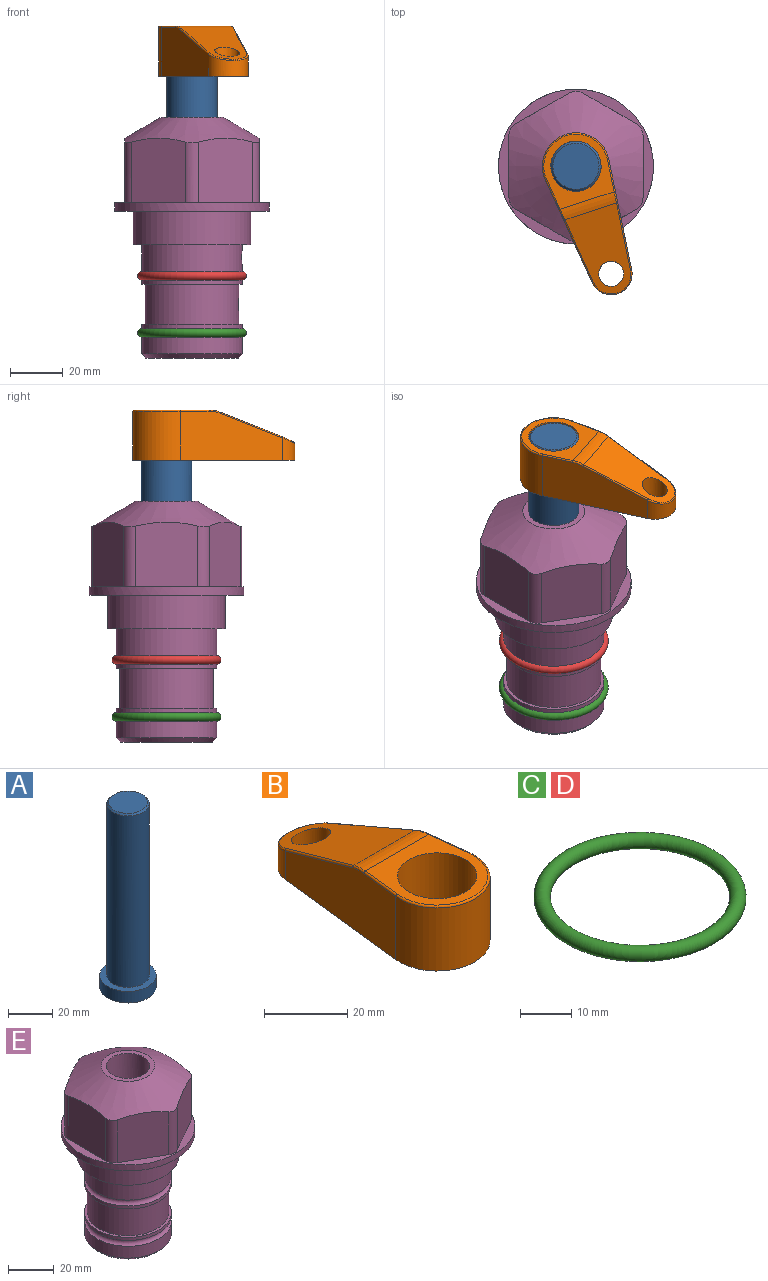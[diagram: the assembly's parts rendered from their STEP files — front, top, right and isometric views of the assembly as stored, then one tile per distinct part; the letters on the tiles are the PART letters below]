
ASSEMBLY  parts=5 mates=3
PART A: 6 faces, bbox 25.4x25.4x101.6 mm
  f0: plane 17.46x17.46mm, normal (0,0,1), area 239.5mm2, adj f5
  f1: plane 25.4x25.4mm, normal (0,0,-1), area 506.7mm2, adj f2
  f2: cylinder r=12.7mm len=25.4mm, axis (0,0,1), area 506.7mm2, adj f1,f3
  f3: plane 25.4x25.4mm, normal (0,0,1), area 221.7mm2, adj f2,f4
  f4: cylinder r=9.53mm len=94.46mm, axis (0,0,1), area 5653mm2, adj f3,f5
  f5: cone r=8.73mm half-angle=45deg, axis (0,0,-1), area 64.4mm2, adj f0,f4
PART B: 44 faces, bbox 27.5x64.5x19.1 mm
  f0: plane 2.3x0.95mm, normal (0,0,-1), area 1mm2, adj f25,f30,f34
  f1: plane 63.5x25.4mm, normal (0,0,-1), area 561.7mm2, adj f2,f3,f4,f5,f6,f7,f19,f20
  f2: cylinder r=12.7mm len=25.4mm, axis (0,0,-1), area 792.2mm2, adj f1,f3,f5,f13
  f3: plane 42.33x18.54mm, normal (0.99,0.11,0), area 647mm2, adj f1,f2,f4,f11,f12,f14
  f4: cylinder r=7.94mm len=15.78mm, axis (0,0,-1), area 158.6mm2, adj f1,f3,f5,f16
  f5: plane 42.33x18.54mm, normal (-0.99,0.11,0), area 647mm2, adj f1,f2,f4,f15,f17,f18
  f6: cylinder r=9.53mm len=19.05mm, axis (0,0,-1), area 1140.1mm2, adj f1,f8
  f7: cylinder r=4.76mm len=10.98mm, axis (0,0,-1), area 276.1mm2, adj f1,f9
  f8: plane 25.83x24.38mm, normal (0,0,1), area 262.2mm2, adj f6,f10,f11,f13,f15
  f9: plane 32.49x20.55mm, normal (0,0.34,0.94), area 489.9mm2, adj f7,f10,f14,f16,f18
  f10: cylinder r=12.7mm len=21.49mm, axis (-1,0,0), area 93.2mm2, adj f8,f9,f12,f17
  f11: cylinder r=0.51mm len=12.34mm, axis (0.11,-0.99,0), area 9.9mm2, adj f3,f8,f12,f13
  f12: bspline ~7.62x1.64mm, area 3.5mm2, adj f3,f10,f11,f14
  f13: torus R=12.19mm, axis (0,0,1), area 33.6mm2, adj f2,f8,f11,f15
  f14: cylinder r=0.51mm len=26.01mm, axis (0.1,-0.93,0.34), area 21.6mm2, adj f3,f9,f12,f16
  f15: cylinder r=0.51mm len=12.34mm, axis (0.11,0.99,0), area 9.9mm2, adj f5,f8,f13,f17
  f16: bspline ~15.78x7.05mm, area 15.7mm2, adj f4,f9,f14,f18
  f17: bspline ~7.62x1.64mm, area 3.5mm2, adj f5,f10,f15,f18
  f18: cylinder r=0.51mm len=26.01mm, axis (0.1,0.93,-0.34), area 21.6mm2, adj f5,f9,f16,f17
  f19: plane 21.6x14.29mm, normal (-0.99,-0.11,0), area 242.6mm2, adj f1,f26,f28,f34,f36,f38
  f20: plane 21.6x14.29mm, normal (0.99,-0.11,0), area 242.6mm2, adj f1,f27,f29,f37,f39,f41
  f21: cylinder r=12.7mm len=14.29mm, axis (0,0,-1), area 173.2mm2, adj f1,f26,f27,f30,f31,f33
  f22: cylinder r=7.94mm len=7.63mm, axis (0,0,-1), area 53.8mm2, adj f1,f28,f29,f42
  f23: plane 2.3x0.95mm, normal (0,0,-1), area 1mm2, adj f25,f33,f37
  f24: plane 17.94x12.32mm, normal (0,-0.34,-0.94), area 191.2mm2, adj f25,f38,f41,f42
  f25: cylinder r=9.53mm len=12.93mm, axis (-1,0,0), area 37.5mm2, adj f0,f23,f24,f31,f36,f39
  f26: cylinder r=1.59mm len=14.29mm, axis (0,0,-1), area 49mm2, adj f1,f19,f21,f32
  f27: cylinder r=1.59mm len=14.29mm, axis (0,0,-1), area 49mm2, adj f1,f20,f21,f35
  f28: cylinder r=1.59mm len=7.28mm, axis (0,0,-1), area 22.1mm2, adj f1,f19,f22,f40
  f29: cylinder r=1.59mm len=7.28mm, axis (0,0,-1), area 22.1mm2, adj f1,f20,f22,f43
  f30: torus R=14.29mm, axis (0,0,1), area 5.8mm2, adj f0,f21,f31,f32
  f31: bspline ~11.06x2.73mm, area 20.8mm2, adj f21,f25,f30,f33
  f32: sphere r=1.59mm, area 5.4mm2, adj f26,f30,f34
  f33: torus R=14.29mm, axis (0,0,1), area 5.8mm2, adj f21,f23,f31,f35
  f34: cylinder r=1.59mm len=1.68mm, axis (-0.11,0.99,0), area 2.4mm2, adj f0,f19,f32,f36
  f35: sphere r=1.59mm, area 5.4mm2, adj f27,f33,f37
  f36: bspline ~5.82x2.33mm, area 7.7mm2, adj f19,f25,f34,f38
  f37: cylinder r=1.59mm len=1.68mm, axis (0.11,0.99,0), area 2.4mm2, adj f20,f23,f35,f39
  f38: cylinder r=1.59mm len=18.33mm, axis (0.1,-0.93,0.34), area 46.7mm2, adj f19,f24,f36,f40
  f39: bspline ~5.82x2.33mm, area 7.7mm2, adj f20,f25,f37,f41
  f40: sphere r=1.59mm, area 3.6mm2, adj f28,f38,f42
  f41: cylinder r=1.59mm len=18.33mm, axis (0.1,0.93,-0.34), area 46.7mm2, adj f20,f24,f39,f43
  f42: bspline ~8.31x1.84mm, area 15.3mm2, adj f22,f24,f40,f43
  f43: sphere r=1.59mm, area 3.6mm2, adj f29,f41,f42
PART C: 1 faces, bbox 44.7x44.7x3.2 mm
  f0: torus R=19.05mm, axis (0,0,1), area 1193.9mm2
PART D: same geometry as C
PART E: 36 faces, bbox 58.7x58.7x91.2 mm
  f0: cylinder r=17.78mm len=35.56mm, axis (0,0,1), area 1670.8mm2, adj f23,f24,f31
  f1: cylinder r=19.05mm len=38.1mm, axis (0,0,1), area 1191.9mm2, adj f26,f27,f30
  f2: plane 58.66x58.66mm, normal (0,0,-1), area 1150.6mm2, adj f3,f28
  f3: cylinder r=29.33mm len=58.66mm, axis (0,0,-1), area 585.1mm2, adj f2,f4
  f4: plane 58.66x58.66mm, normal (0,0,1), area 475.9mm2, adj f3,f5,f6,f7,f8,f9,f10,f11
  f5: plane 24.5x20.32mm, normal (-0.5,0.87,0), area 562.8mm2, adj f4,f15,f16,f17
  f6: plane 24.5x20.32mm, normal (0.5,0.87,0), area 562.8mm2, adj f4,f14,f15,f17
  f7: plane 24.5x23.48mm, normal (1,0,0), area 562.8mm2, adj f4,f13,f14,f17
  f8: plane 24.5x20.32mm, normal (0.5,-0.87,0), area 562.8mm2, adj f4,f12,f13,f17
  f9: plane 24.5x20.32mm, normal (-0.5,-0.87,0), area 562.8mm2, adj f4,f11,f12,f17
  f10: plane 24.5x23.48mm, normal (-1,0,0), area 562.8mm2, adj f4,f11,f16,f17
  f11: cylinder r=5.08mm len=23.01mm, axis (0,0,-1), area 121.2mm2, adj f4,f9,f10,f17
  f12: cylinder r=5.08mm len=23.01mm, axis (0,0,-1), area 121.2mm2, adj f4,f8,f9,f17
  f13: cylinder r=5.08mm len=23.01mm, axis (0,0,-1), area 121.2mm2, adj f4,f7,f8,f17
  f14: cylinder r=5.08mm len=23.01mm, axis (0,0,-1), area 121.2mm2, adj f4,f6,f7,f17
  f15: cylinder r=5.08mm len=23.01mm, axis (0,0,-1), area 121.2mm2, adj f4,f5,f6,f17
  f16: cylinder r=5.08mm len=23.01mm, axis (0,0,-1), area 121.2mm2, adj f4,f5,f10,f17
  f17: cone r=11.73mm half-angle=60deg, axis (0,0,-1), area 2071.8mm2, adj f5,f6,f7,f8,f9,f10,f11,f12
  f18: plane 23.46x23.46mm, normal (0,0,1), area 147.4mm2, adj f17,f35
  f19: plane 34.93x34.93mm, normal (0,0,-1), area 958mm2, adj f29
  f20: cylinder r=19.05mm len=38.1mm, axis (0,0,1), area 760.1mm2, adj f21,f29
  f21: torus R=19.05mm, axis (0,0,1), area 565.3mm2, adj f20,f22
  f22: cylinder r=19.05mm len=38.1mm, axis (0,0,1), area 190mm2, adj f21,f23
  f23: plane 38.1x38.1mm, normal (0,0,1), area 146.9mm2, adj f0,f22
  f24: plane 38.1x38.1mm, normal (0,0,-1), area 146.9mm2, adj f0,f25
  f25: cylinder r=19.05mm len=38.1mm, axis (0,0,1), area 190mm2, adj f24,f26
  f26: torus R=19.05mm, axis (0,0,1), area 565.3mm2, adj f1,f25
  f27: plane 44.45x44.45mm, normal (0,0,-1), area 411.7mm2, adj f1,f28
  f28: cylinder r=22.23mm len=44.45mm, axis (0,0,1), area 1773.5mm2, adj f2,f27
  f29: cone r=19.05mm half-angle=45deg, axis (0,0,1), area 257.5mm2, adj f19,f20
  f30: cylinder r=3.17mm len=6.75mm, axis (-1,0,0), area 128mm2, adj f1,f33
  f31: cylinder r=3.17mm len=6.35mm, axis (-1,0,0), area 102.5mm2, adj f0,f33
  f32: plane 25.4x25.4mm, normal (0,0,1), area 506.7mm2, adj f33
  f33: cylinder r=12.7mm len=66.42mm, axis (0,0,-1), area 5236.2mm2, adj f30,f31,f32,f34
  f34: cone r=9.53mm half-angle=30deg, axis (0,0,-1), area 443.4mm2, adj f33,f35
  f35: cylinder r=9.53mm len=19.05mm, axis (0,0,-1), area 849mm2, adj f18,f34
PLACE A rot(axis=(0,0,-1),71.9deg) t=(0,0,-3.51)mm
PLACE B rot(axis=(0,0,-1),161.9deg) t=(0,0,51.1)mm
PLACE C t=(0,0,-21.59)mm
PLACE D at identity
PLACE E at identity fixed
MATE fastened C.f0 <-> E.f0  axis (0,0,1) through (0,0,-46.1)mm
MATE cylindrical A.f2 <-> E.f0  axis (0,0,1) through (0,0,22.12)mm
MATE fastened B.f2 <-> A.f2  axis (0,0,1) through (0,0,70.15)mm
